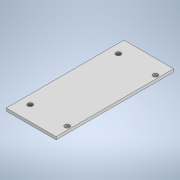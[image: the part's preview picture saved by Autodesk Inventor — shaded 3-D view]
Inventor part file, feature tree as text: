
AUTODESK INVENTOR PART (.ipt)
format: ipt  version: 2021 (Build 250183000, 183)  size: 115,200 bytes
history: native  units: mm
features: other x1, extrude x1, sketch x1
ambient origin geometry x8: Origin, YZ Plane, XZ Plane, XY Plane, X Axis, Y Axis, Z Axis, Center Point
bodies: Body1 (feature_tree)
feature tree (3):
  other  "Sólido1"
  extrude  "Extrusión1"  Depth=35.5mm
  sketch  "Boceto1"  dims[d0=84.0mm d1=35.5mm d2=3.5mm d3=6.5mm d4=10.5mm d5=3.5mm d6=26.5mm d7=84.0mm d8=84.0mm d9=63.0mm d10=2.0mm d11=0.0mm]
